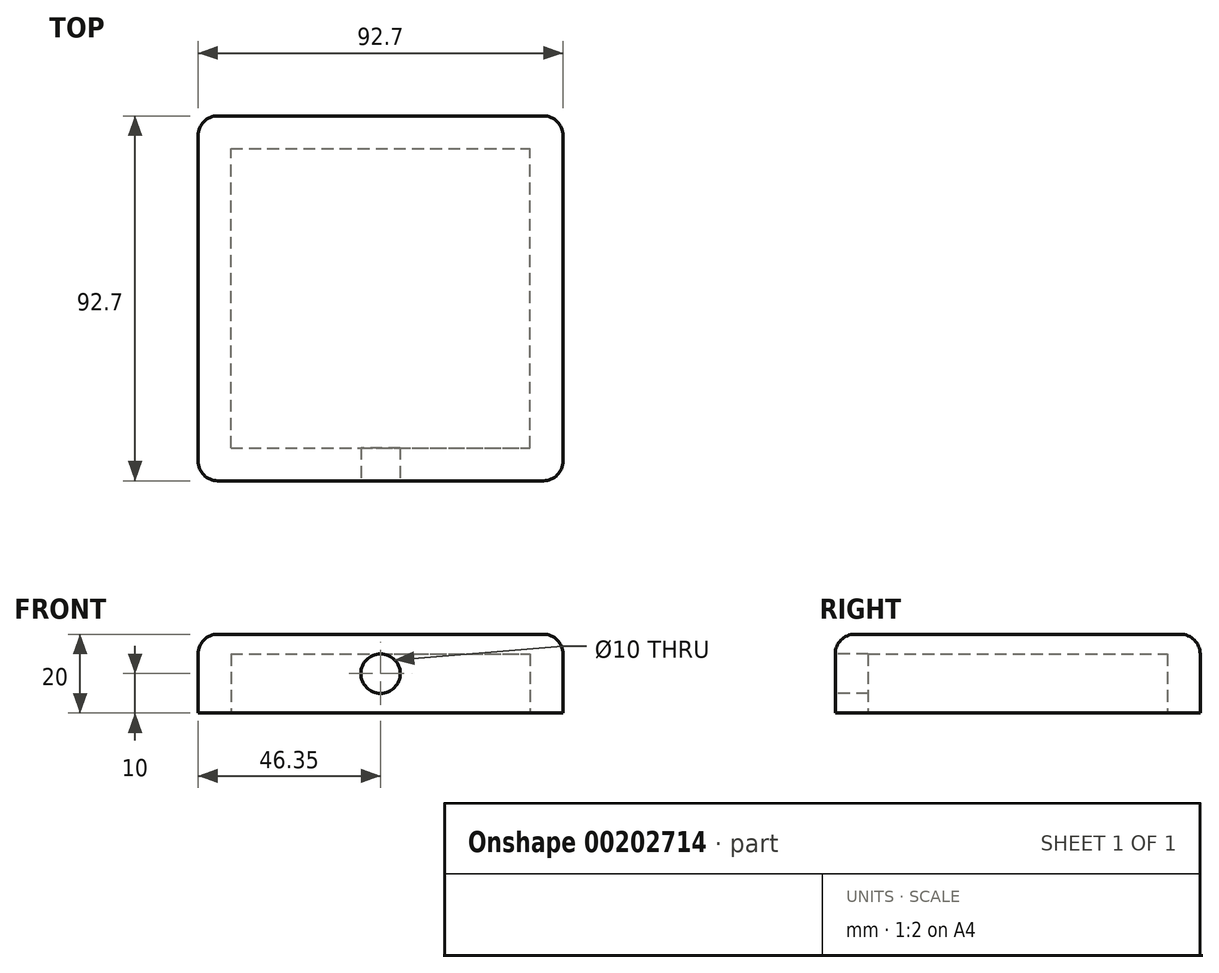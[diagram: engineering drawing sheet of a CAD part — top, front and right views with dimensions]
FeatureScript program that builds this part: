
annotation { "Feature Type Name" : "Feature", "Feature Type Description" : "" }
export const myFeature = defineFeature(function(context is Context, id is Id, definition is map)
    precondition{}
    {
        {
            var Q0;
            Q0=qCreatedBy(makeId("Top.planeOp"),FACE);
            var sketch = newSketch(context, id + "F0", { "sketchPlane" : qUnion([Q0])});
            skLineSegment(sketch, "E0.bottom", {"start": v(46.35, 46.35) * mm, "end": v(-46.35, 46.35) * mm});
            skLineSegment(sketch, "E0.top", {"start": v(46.35, -46.35) * mm, "end": v(-46.35, -46.35) * mm});
            skLineSegment(sketch, "E0.left", {"start": v(46.35, 46.35) * mm, "end": v(46.35, -46.35) * mm});
            skLineSegment(sketch, "E0.right", {"start": v(-46.35, 46.35) * mm, "end": v(-46.35, -46.35) * mm});
            skPoint(sketch, "E0.middle", {"position": v(0, 0) * mm});
            skLineSegment(sketch, "E1.bottom", {"start": v(-38, -38) * mm, "end": v(38, -38) * mm});
            skLineSegment(sketch, "E1.top", {"start": v(-38, 38) * mm, "end": v(38, 38) * mm});
            skLineSegment(sketch, "E1.left", {"start": v(-38, -38) * mm, "end": v(-38, 38) * mm});
            skLineSegment(sketch, "E1.right", {"start": v(38, -38) * mm, "end": v(38, 38) * mm});
            skSolve(sketch);
        }
        {
            var Q0;
            Q0=makeQuery(id+"F0.imprint","IMPRINT",FACE,{"disambiguationData":[TD([[makeQuery(id+"F0.imprint","IMPRINT",EDGE,{"derivedFrom":sQuery(id+"F0.wireOp",EDGE,"E0.bottom")}),1.0]])]});
            var Q1;
            Q1=makeQuery(id+"F0.imprint","IMPRINT",FACE,{"disambiguationData":[TD([[makeQuery(id+"F0.imprint","IMPRINT",EDGE,{"derivedFrom":sQuery(id+"F0.wireOp",EDGE,"E1.bottom")}),1.0]])]});
            extrude(context, id + "F1", {"entities" : qUnion([Q0, Q1]), "depth" : 20 * mm});
        }
        {
            var Q0;
            Q0=makeQuery(id+"F1.opExtrude","CAP_EDGE",EDGE,{"disambiguationData":[OSD([sQuery(id+"F0.wireOp",EDGE,"E0.right")])],"isStart":false});
            var Q1;
            Q1=makeQuery(id+"F1.opExtrude","CAP_EDGE",EDGE,{"disambiguationData":[OSD([sQuery(id+"F0.wireOp",EDGE,"E0.bottom")])],"isStart":false});
            var Q2;
            Q2=makeQuery(id+"F1.opExtrude","CAP_EDGE",EDGE,{"disambiguationData":[OSD([sQuery(id+"F0.wireOp",EDGE,"E0.left")])],"isStart":false});
            var Q3;
            Q3=makeQuery(id+"F1.opExtrude","CAP_EDGE",EDGE,{"disambiguationData":[OSD([sQuery(id+"F0.wireOp",EDGE,"E0.top")])],"isStart":false});
            var Q4;
            Q4=makeQuery(id+"F1.opExtrude","SWEPT_EDGE",EDGE,{"disambiguationData":[OSD([sQuery(id+"F0.wireOp",EDGE,"E0.top"),sQuery(id+"F0.wireOp",EDGE,"E0.left")])]});
            var Q5;
            Q5=makeQuery(id+"F1.opExtrude","SWEPT_EDGE",EDGE,{"disambiguationData":[OSD([sQuery(id+"F0.wireOp",EDGE,"E0.top"),sQuery(id+"F0.wireOp",EDGE,"E0.right")])]});
            var Q6;
            Q6=makeQuery(id+"F1.opExtrude","SWEPT_EDGE",EDGE,{"disambiguationData":[OSD([sQuery(id+"F0.wireOp",EDGE,"E0.bottom"),sQuery(id+"F0.wireOp",EDGE,"E0.left")])]});
            var Q7;
            Q7=makeQuery(id+"F1.opExtrude","SWEPT_EDGE",EDGE,{"disambiguationData":[OSD([sQuery(id+"F0.wireOp",EDGE,"E0.bottom"),sQuery(id+"F0.wireOp",EDGE,"E0.right")])]});
            fillet(context, id + "F2", {"entities" : qUnion([Q0, Q1, Q2, Q3, Q4, Q5, Q6, Q7]), "radius" : 5 * mm, "tangentPropagation" : true, "allowEdgeOverflow" : false});
        }
        {
            var Q0;
            Q0=makeQuery(id+"F1.opExtrude","SWEPT_FACE",FACE,{"disambiguationData":[OSD([sQuery(id+"F0.wireOp",EDGE,"E0.top")])]});
            var sketch = newSketch(context, id + "F3", { "sketchPlane" : qUnion([Q0])});
            skLineSegment(sketch, "E2", {"start": v(0, 0) * mm, "end": v(0, 10) * mm});
            skPoint(sketch, "E2.endSnap0", {"position": v(0, 0) * mm});
            skCircle(sketch, "E3", {"center": v(0, 10) * mm, "radius": 5 * mm});
            skSolve(sketch);
        }
        {
            var Q0;
            Q0=makeQuery(id+"F0.imprint","IMPRINT",FACE,{"disambiguationData":[TD([[makeQuery(id+"F0.imprint","IMPRINT",EDGE,{"derivedFrom":sQuery(id+"F0.wireOp",EDGE,"E1.bottom")}),1.0]])]});
            extrude(context, id + "F4", {"entities" : qUnion([Q0]), "operationType" : NewBodyOperationType.REMOVE, "depth" : 15 * mm});
        }
        {
            var Q0;
            {var subQ0=sQuery(id+"F3.wireOp",EDGE,"E3");var subQ1=makeQuery(id+"F3.imprint","INTERSECT",VERTEX,{"derivedFrom":[sQuery(id+"F3.wireOp",EDGE,"E2"),subQ0]});Q0=makeQuery(id+"F3.imprint","IMPRINT",FACE,{"disambiguationData":[TD([[makeQuery(id+"F3.imprint","IMPRINT",EDGE,{"disambiguationData":[TD([[subQ1,1.0]])],"derivedFrom":subQ0}),1.0]])]});}
            var Q1;
            Q1=makeQuery(id+"F4.boolean.opBoolean","COPY",FACE,{"derivedFrom":makeQuery(id+"F4.opExtrude","SWEPT_FACE",FACE,{"disambiguationData":[OSD([sQuery(id+"F0.wireOp",EDGE,"E1.bottom")])]})});
            extrude(context, id + "F5", {"entities" : qUnion([Q0]), "operationType" : NewBodyOperationType.REMOVE, "endBound" : BoundingType.UP_TO_SURFACE, "oppositeDirection" : true, "endBoundEntityFace" : qUnion([Q1]), "depth" : 25 * mm});
        }
    });
